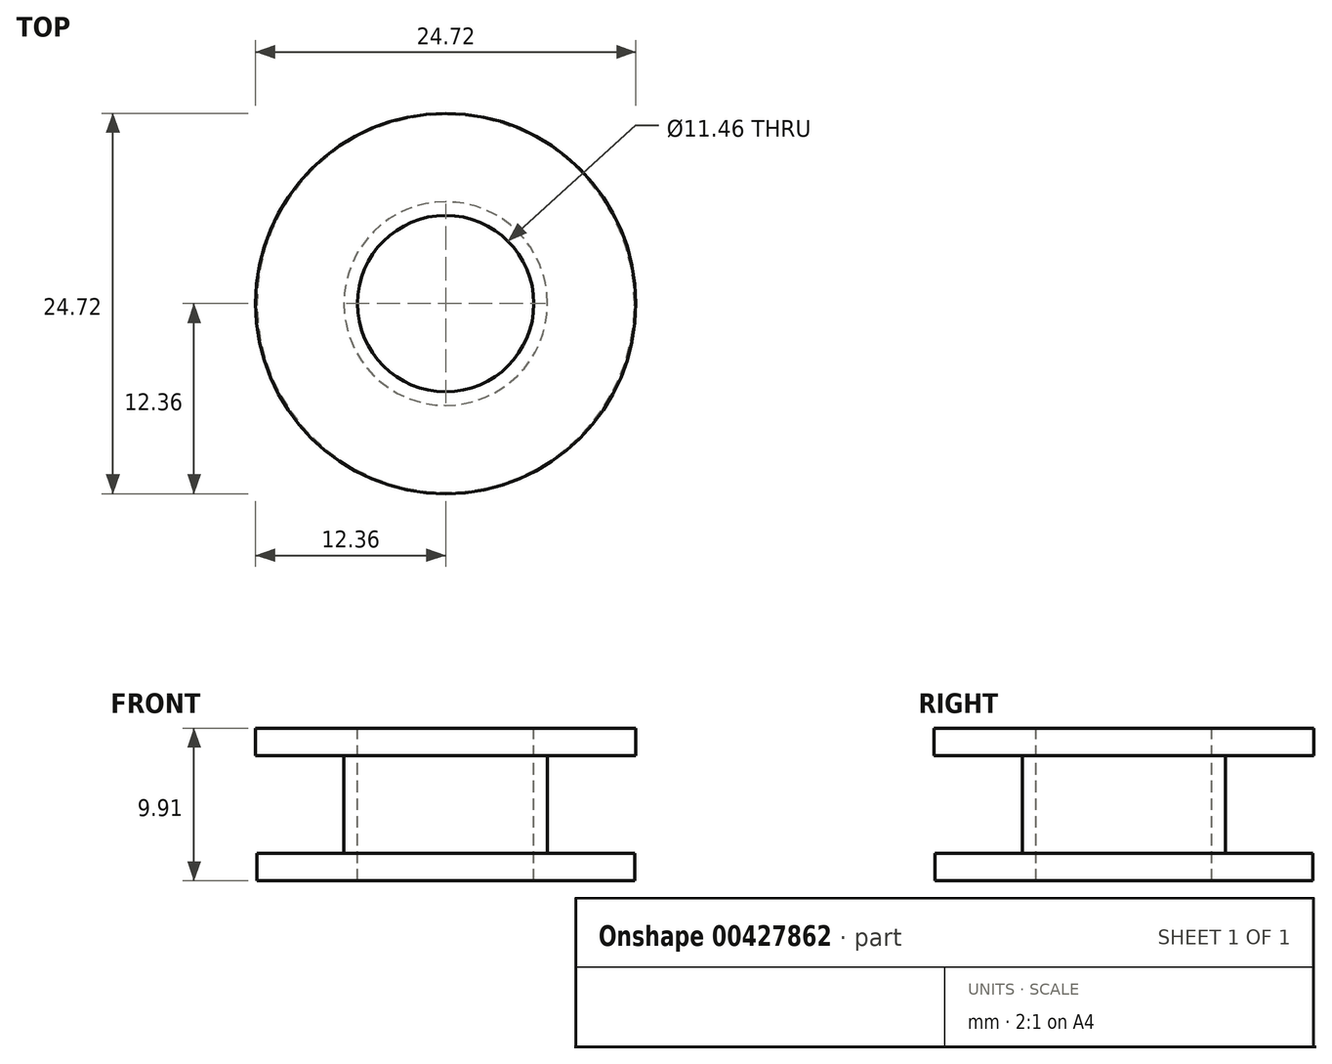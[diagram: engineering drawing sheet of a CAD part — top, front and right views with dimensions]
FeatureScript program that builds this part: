
annotation { "Feature Type Name" : "Feature", "Feature Type Description" : "" }
export const myFeature = defineFeature(function(context is Context, id is Id, definition is map)
    precondition{}
    {
        {
            var Q0;
            Q0=qCreatedBy(makeId("Top.planeOp"),FACE);
            var sketch = newSketch(context, id + "F0", { "sketchPlane" : qUnion([Q0])});
            skCircle(sketch, "E0", {"center": v(0, 0) * mm, "radius": 12.28 * mm});
            skSolve(sketch);
        }
        {
            var Q0;
            Q0 = qSketchRegion(id + "F0", true);
            extrude(context, id + "F1", {"entities" : qUnion([Q0]), "depth" : 1.78 * mm});
        }
        {
            var Q0;
            Q0=qCreatedBy(makeId("Top.planeOp"),FACE);
            var sketch = newSketch(context, id + "F2", { "sketchPlane" : qUnion([Q0])});
            skCircle(sketch, "E1", {"center": v(0, 0) * mm, "radius": 6.62 * mm});
            skSolve(sketch);
        }
        {
            var Q0;
            Q0 = qSketchRegion(id + "F2", true);
            extrude(context, id + "F3", {"entities" : qUnion([Q0]), "operationType" : NewBodyOperationType.ADD, "depth" : 8.13 * mm});
        }
        {
            var Q0;
            Q0=makeQuery(id+"F3.opExtrude","CAP_FACE",FACE,{"disambiguationData":[OSD([sQuery(id+"F2.wireOp",EDGE,"E1")])],"isStart":false});
            var sketch = newSketch(context, id + "F4", { "sketchPlane" : qUnion([Q0])});
            skCircle(sketch, "E2", {"center": v(0, 0) * mm, "radius": 12.36 * mm});
            skSolve(sketch);
        }
        {
            var Q0;
            Q0 = qSketchRegion(id + "F4", true);
            extrude(context, id + "F5", {"entities" : qUnion([Q0]), "operationType" : NewBodyOperationType.ADD, "depth" : 1.78 * mm});
        }
        {
            var Q0;
            Q0=makeQuery(id+"F5.opExtrude","CAP_FACE",FACE,{"disambiguationData":[OSD([sQuery(id+"F4.wireOp",EDGE,"E2")])],"isStart":false});
            var sketch = newSketch(context, id + "F6", { "sketchPlane" : qUnion([Q0])});
            skCircle(sketch, "E3", {"center": v(0, 0) * mm, "radius": 5.73 * mm});
            skSolve(sketch);
        }
        {
            var Q0;
            Q0 = qSketchRegion(id + "F6", true);
            extrude(context, id + "F7", {"entities" : qUnion([Q0]), "operationType" : NewBodyOperationType.REMOVE, "endBound" : BoundingType.THROUGH_ALL, "oppositeDirection" : true, "depth" : 25.4 * mm});
        }
    });
